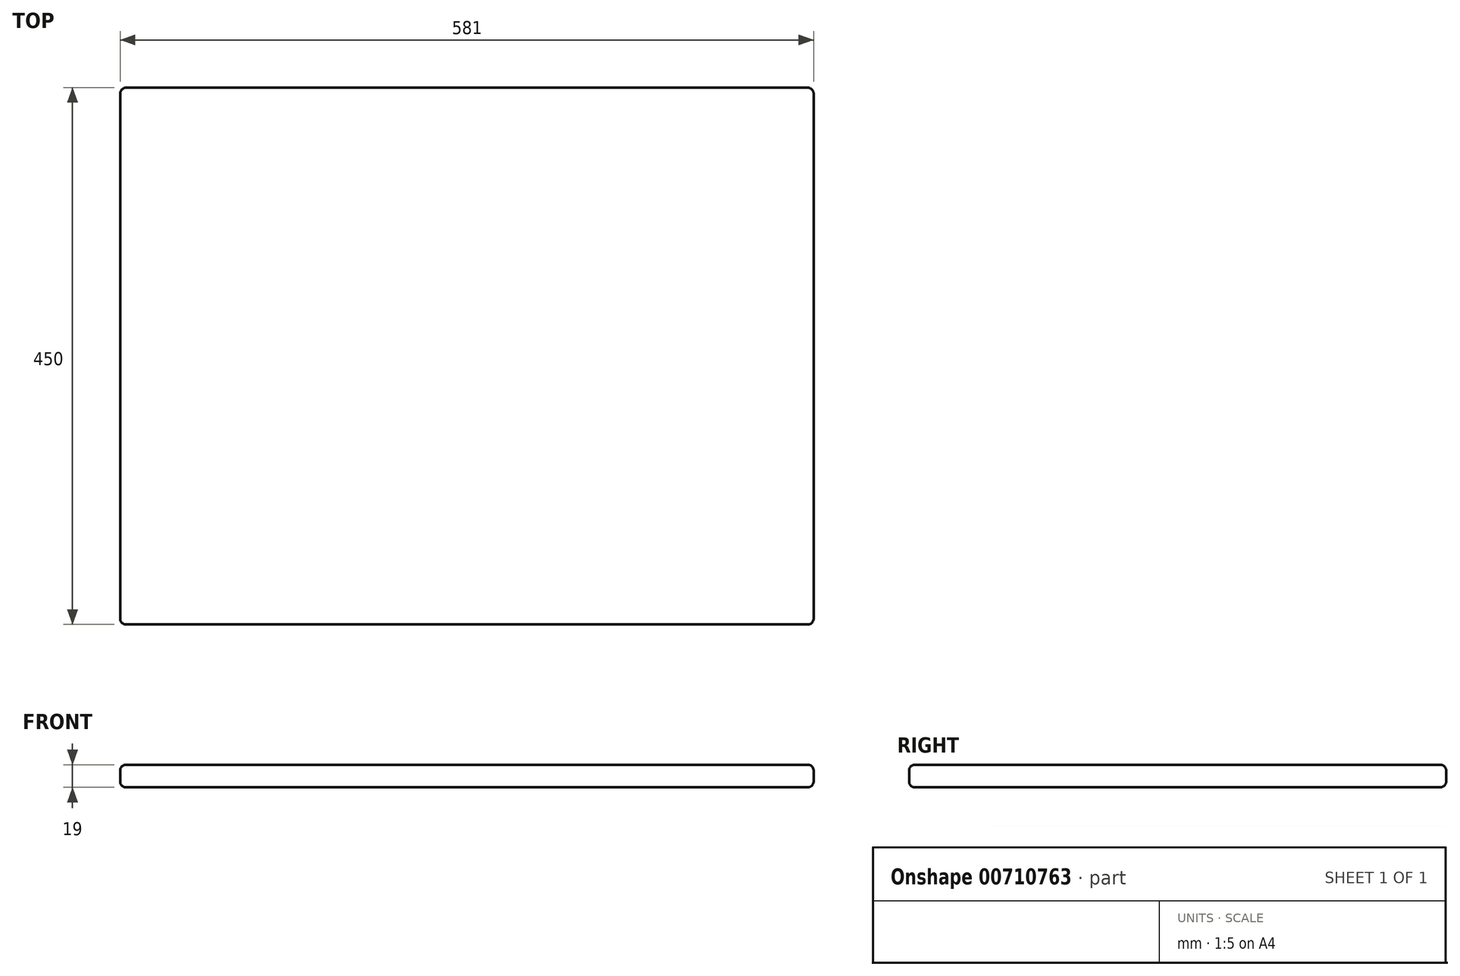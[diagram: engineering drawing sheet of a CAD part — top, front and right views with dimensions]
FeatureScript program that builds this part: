
annotation { "Feature Type Name" : "Feature", "Feature Type Description" : "" }
export const myFeature = defineFeature(function(context is Context, id is Id, definition is map)
    precondition{}
    {
        {
            var Q0;
            Q0=qCreatedBy(makeId("Top.planeOp"),FACE);
            var sketch = newSketch(context, id + "F0", { "sketchPlane" : qUnion([Q0])});
            skLineSegment(sketch, "E0.bottom", {"start": v(-417, 234.06) * mm, "end": v(164, 234.06) * mm});
            skLineSegment(sketch, "E0.top", {"start": v(-417, -215.94) * mm, "end": v(164, -215.94) * mm});
            skLineSegment(sketch, "E0.left", {"start": v(-417, 234.06) * mm, "end": v(-417, -215.94) * mm});
            skLineSegment(sketch, "E0.right", {"start": v(164, 234.06) * mm, "end": v(164, -215.94) * mm});
            skSolve(sketch);
        }
        {
            var Q0;
            Q0=makeQuery(id+"F0.imprint","IMPRINT",FACE,{"disambiguationData":[TD([[makeQuery(id+"F0.imprint","IMPRINT",EDGE,{"derivedFrom":sQuery(id+"F0.wireOp",EDGE,"E0.bottom")}),-1.0]])]});
            extrude(context, id + "F1", {"entities" : qUnion([Q0]), "depth" : 19 * mm, "offsetDistance" : 25 * mm});
        }
        {
            var Q0;
            Q0=makeQuery(id+"F1.opExtrude","SWEPT_EDGE",EDGE,{"disambiguationData":[OSD([sQuery(id+"F0.wireOp",EDGE,"E0.top"),sQuery(id+"F0.wireOp",EDGE,"E0.right")])]});
            var Q1;
            Q1=makeQuery(id+"F1.opExtrude","CAP_EDGE",EDGE,{"disambiguationData":[OSD([sQuery(id+"F0.wireOp",EDGE,"E0.top")])],"isStart":true});
            var Q2;
            Q2=makeQuery(id+"F1.opExtrude","CAP_EDGE",EDGE,{"disambiguationData":[OSD([sQuery(id+"F0.wireOp",EDGE,"E0.top")])],"isStart":false});
            var Q3;
            Q3=makeQuery(id+"F1.opExtrude","CAP_EDGE",EDGE,{"disambiguationData":[OSD([sQuery(id+"F0.wireOp",EDGE,"E0.right")])],"isStart":false});
            var Q4;
            Q4=makeQuery(id+"F1.opExtrude","SWEPT_EDGE",EDGE,{"disambiguationData":[OSD([sQuery(id+"F0.wireOp",EDGE,"E0.bottom"),sQuery(id+"F0.wireOp",EDGE,"E0.right")])]});
            var Q5;
            Q5=makeQuery(id+"F1.opExtrude","CAP_EDGE",EDGE,{"disambiguationData":[OSD([sQuery(id+"F0.wireOp",EDGE,"E0.bottom")])],"isStart":false});
            var Q6;
            Q6=makeQuery(id+"F1.opExtrude","CAP_EDGE",EDGE,{"disambiguationData":[OSD([sQuery(id+"F0.wireOp",EDGE,"E0.bottom")])],"isStart":true});
            var Q7;
            Q7=makeQuery(id+"F1.opExtrude","SWEPT_EDGE",EDGE,{"disambiguationData":[OSD([sQuery(id+"F0.wireOp",EDGE,"E0.bottom"),sQuery(id+"F0.wireOp",EDGE,"E0.left")])]});
            var Q8;
            Q8=makeQuery(id+"F1.opExtrude","CAP_EDGE",EDGE,{"disambiguationData":[OSD([sQuery(id+"F0.wireOp",EDGE,"E0.left")])],"isStart":false});
            var Q9;
            Q9=makeQuery(id+"F1.opExtrude","CAP_EDGE",EDGE,{"disambiguationData":[OSD([sQuery(id+"F0.wireOp",EDGE,"E0.left")])],"isStart":true});
            var Q10;
            Q10=makeQuery(id+"F1.opExtrude","SWEPT_EDGE",EDGE,{"disambiguationData":[OSD([sQuery(id+"F0.wireOp",EDGE,"E0.top"),sQuery(id+"F0.wireOp",EDGE,"E0.left")])]});
            var Q11;
            Q11=makeQuery(id+"F1.opExtrude","CAP_FACE",FACE,{"disambiguationData":[OSD([sQuery(id+"F0.wireOp",EDGE,"E0.bottom"),sQuery(id+"F0.wireOp",EDGE,"E0.top"),sQuery(id+"F0.wireOp",EDGE,"E0.left"),sQuery(id+"F0.wireOp",EDGE,"E0.right")])],"isStart":true});
            var Q12;
            Q12=makeQuery(id+"F1.opExtrude","CAP_EDGE",EDGE,{"disambiguationData":[OSD([sQuery(id+"F0.wireOp",EDGE,"E0.right")])],"isStart":true});
            var Q13;
            Q13=makeQuery(id+"F1.opExtrude","CAP_FACE",FACE,{"disambiguationData":[OSD([sQuery(id+"F0.wireOp",EDGE,"E0.bottom"),sQuery(id+"F0.wireOp",EDGE,"E0.top"),sQuery(id+"F0.wireOp",EDGE,"E0.left"),sQuery(id+"F0.wireOp",EDGE,"E0.right")])],"isStart":false});
            fillet(context, id + "F2", {"entities" : qUnion([Q0, Q1, Q2, Q3, Q4, Q5, Q6, Q7, Q8, Q9, Q10, Q11, Q12, Q13]), "radius" : 5 * mm, "tangentPropagation" : true, "allowEdgeOverflow" : false});
        }
    });
